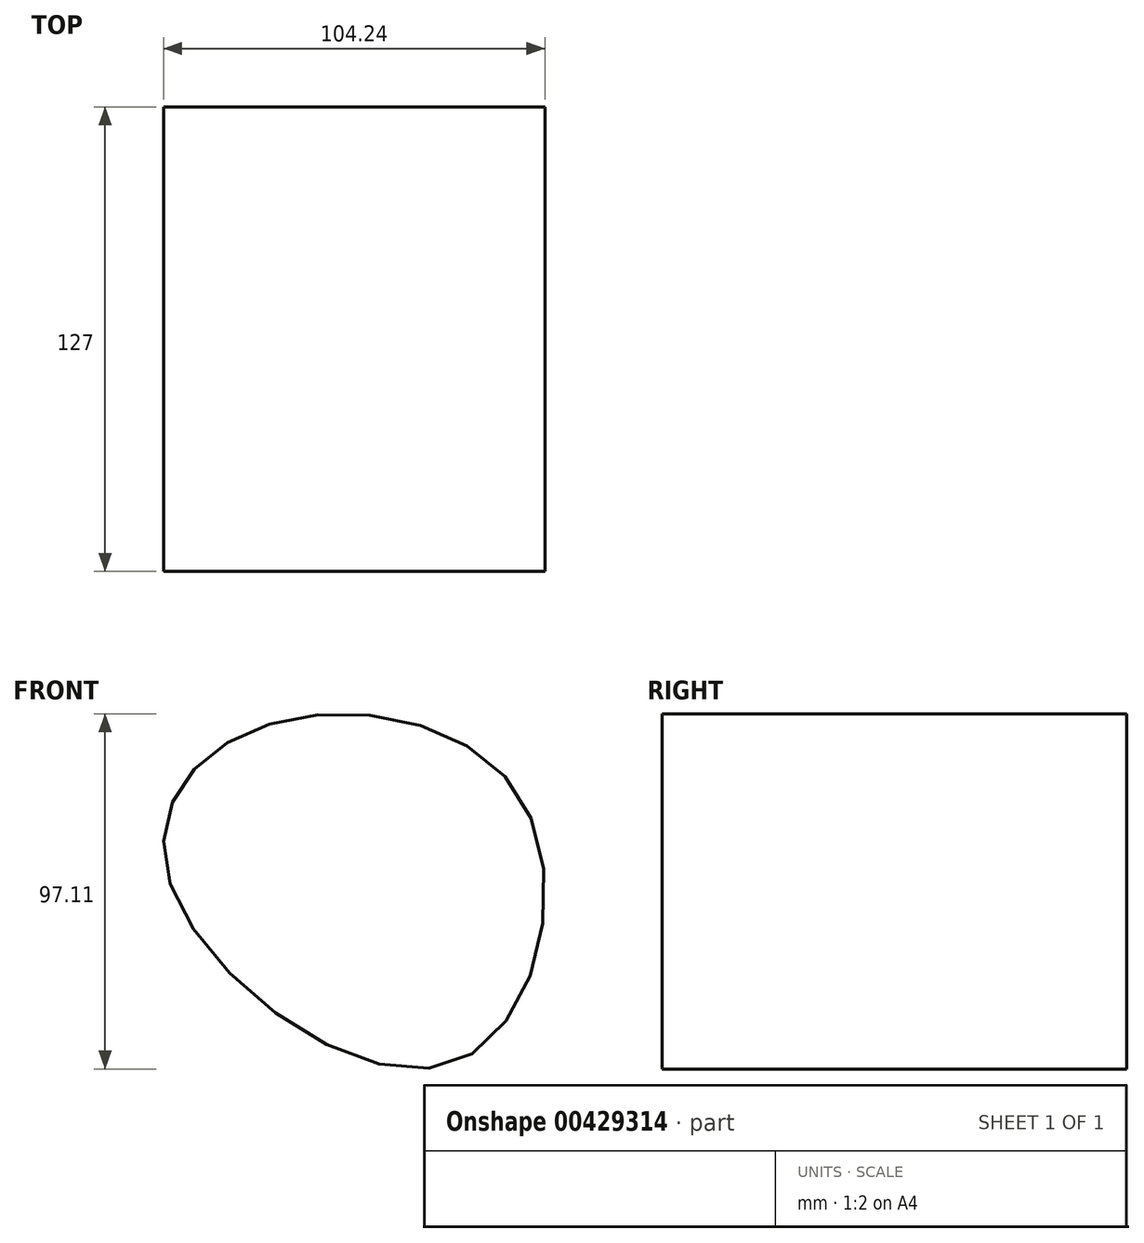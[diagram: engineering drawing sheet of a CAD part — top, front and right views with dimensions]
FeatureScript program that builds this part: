
annotation { "Feature Type Name" : "Feature", "Feature Type Description" : "" }
export const myFeature = defineFeature(function(context is Context, id is Id, definition is map)
    precondition{}
    {
        {
            var Q0;
            Q0=qCreatedBy(makeId("Front.planeOp"),FACE);
            var sketch = newSketch(context, id + "F0", { "sketchPlane" : qUnion([Q0])});
            skFitSpline(sketch, "E0", {"points": [v(-45.73, 5.18) * mm, v(-21.64, 47.85) * mm, v(50.97, 27.2) * mm, v(31, -44.03) * mm, v(-45.73, 5.18) * mm]});
            skSolve(sketch);
        }
        {
            var Q0;
            Q0=makeQuery(id+"F0.imprint","IMPRINT",FACE,{"disambiguationData":[TD([[makeQuery(id+"F0.imprint","IMPRINT",EDGE,{"derivedFrom":sQuery(id+"F0.wireOp",EDGE,"E0")}),-1.0]])]});
            extrude(context, id + "F1", {"entities" : qUnion([Q0]), "endBound" : BoundingType.SYMMETRIC, "depth" : 127 * mm});
        }
    });
